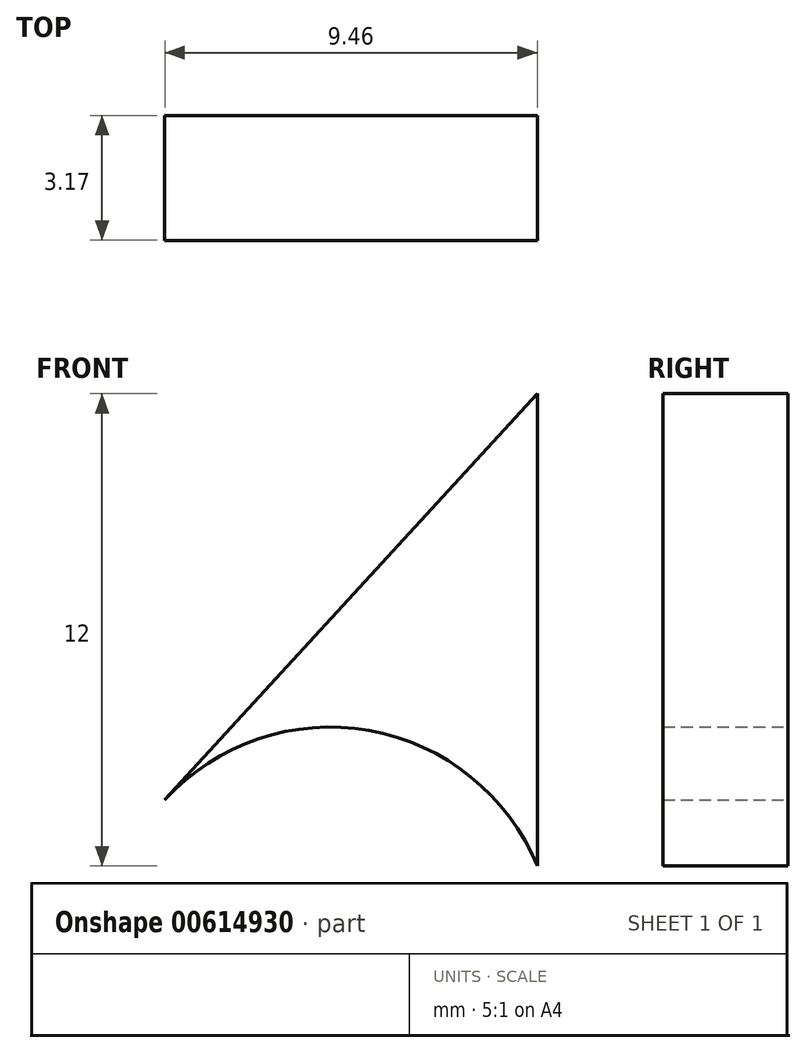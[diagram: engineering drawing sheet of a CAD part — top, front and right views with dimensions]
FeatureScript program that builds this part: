
annotation { "Feature Type Name" : "Feature", "Feature Type Description" : "" }
export const myFeature = defineFeature(function(context is Context, id is Id, definition is map)
    precondition{}
    {
        {
            var Q0;
            Q0=qCreatedBy(makeId("Front.planeOp"),FACE);
            var sketch = newSketch(context, id + "F0", { "sketchPlane" : qUnion([Q0])});
            skLineSegment(sketch, "E0", {"start": v(0, 0) * mm, "end": v(-30, 0) * mm});
            skCircle(sketch, "E1", {"center": v(-30, 0) * mm, "radius": 3.1 * mm});
            skLineSegment(sketch, "E2", {"start": v(0, 0) * mm, "end": v(30, 0) * mm});
            skCircle(sketch, "E3", {"center": v(30, 0) * mm, "radius": 3.1 * mm});
            skLineSegment(sketch, "E4.bottom", {"start": v(47.4, 12.78) * mm, "end": v(-37.4, 12.78) * mm});
            skLineSegment(sketch, "E4.top", {"start": v(37.4, -12.78) * mm, "end": v(-37.4, -12.78) * mm});
            skLineSegment(sketch, "E4.left", {"start": v(47.4, 12.78) * mm, "end": v(47.4, -2.78) * mm});
            skLineSegment(sketch, "E4.right", {"start": v(-47.4, 2.78) * mm, "end": v(-47.4, -2.78) * mm});
            skPoint(sketch, "E4.middle", {"position": v(0, 0) * mm});
            skPoint(sketch, "E5.visualSharp", {"position": v(-47.4, -12.78) * mm});
            skArc(sketch, "E5.filletArc", {"start": v(-47.4, -2.78) * mm, "mid": v(-44.47, -9.85) * mm, "end": v(-37.4, -12.78) * mm});
            skPoint(sketch, "E6.visualSharp", {"position": v(-47.4, 12.78) * mm});
            skArc(sketch, "E6.filletArc", {"start": v(-37.4, 12.78) * mm, "mid": v(-44.47, 9.85) * mm, "end": v(-47.4, 2.78) * mm});
            skPoint(sketch, "E7.visualSharp", {"position": v(47.4, -12.78) * mm});
            skArc(sketch, "E7.filletArc", {"start": v(37.4, -12.78) * mm, "mid": v(44.47, -9.85) * mm, "end": v(47.4, -2.78) * mm});
            skLineSegment(sketch, "E8", {"start": v(47.4, 60.18) * mm, "end": v(47.4, 12.78) * mm});
            skLineSegment(sketch, "E9", {"start": v(47.4, 60.18) * mm, "end": v(37.94, 49.86) * mm});
            skArc(sketch, "E10", {"start": v(-37.4, 12.78) * mm, "mid": v(4.58, 22.56) * mm, "end": v(37.94, 49.86) * mm});
            skLineSegment(sketch, "E11", {"start": v(47.4, 60.18) * mm, "end": v(47.4, 48.18) * mm});
            skLineSegment(sketch, "E12", {"start": v(30, 0) * mm, "end": v(40.16, 40.75) * mm});
            skCircle(sketch, "E13", {"center": v(40.16, 40.75) * mm, "radius": 3.1 * mm});
            skArc(sketch, "E14", {"start": v(47.4, 48.18) * mm, "mid": v(43.13, 51.62) * mm, "end": v(37.94, 49.86) * mm});
            skSolve(sketch);
        }
        {
            var Q0;
            {var subQ0=sQuery(id+"F0.wireOp",EDGE,"E8");Q0=makeQuery(id+"F0.imprint","IMPRINT",FACE,{"disambiguationData":[TD([[makeQuery(id+"F0.imprint","IMPRINT",EDGE,{"derivedFrom":subQ0}),-1.0]])]});}
            var Q1;
            Q1=makeQuery(id+"F0.imprint","IMPRINT",FACE,{"disambiguationData":[TD([[makeQuery(id+"F0.imprint","IMPRINT",EDGE,{"derivedFrom":sQuery(id+"F0.wireOp",EDGE,"E1")}),1.0]])]});
            extrude(context, id + "F1", {"entities" : qUnion([Q0, Q1]), "depth" : 3.17 * mm, "offsetDistance" : 25 * mm});
        }
    });
